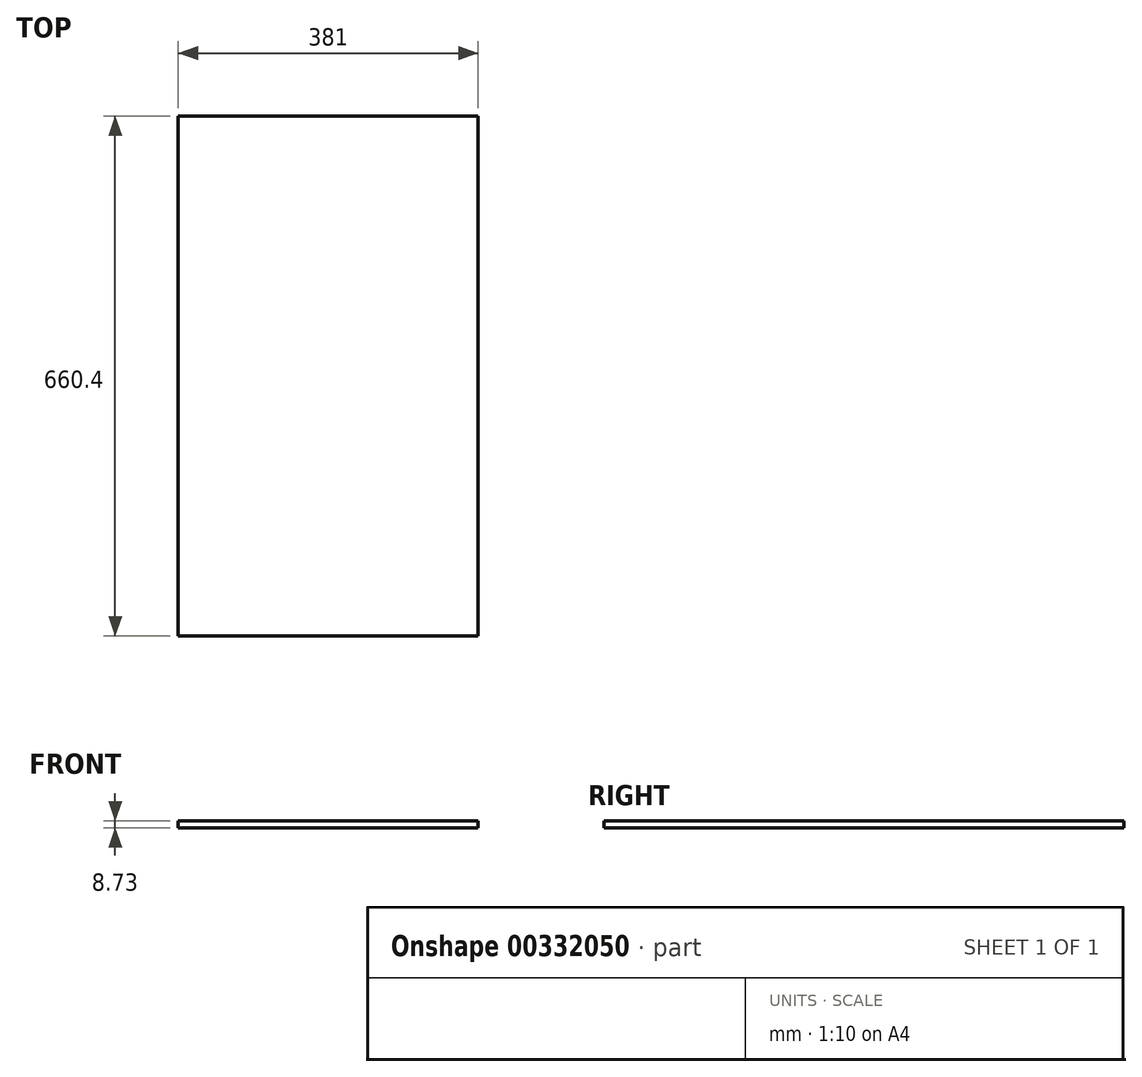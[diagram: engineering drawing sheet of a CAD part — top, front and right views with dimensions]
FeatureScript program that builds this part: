
annotation { "Feature Type Name" : "Feature", "Feature Type Description" : "" }
export const myFeature = defineFeature(function(context is Context, id is Id, definition is map)
    precondition{}
    {
        {
            var Q0;
            Q0=qCreatedBy(makeId("Top.planeOp"),FACE);
            var sketch = newSketch(context, id + "F0", { "sketchPlane" : qUnion([Q0])});
            skLineSegment(sketch, "E0.bottom", {"start": v(190.5, -330.2) * mm, "end": v(-190.5, -330.2) * mm});
            skLineSegment(sketch, "E0.top", {"start": v(190.5, 330.2) * mm, "end": v(-190.5, 330.2) * mm});
            skLineSegment(sketch, "E0.left", {"start": v(190.5, -330.2) * mm, "end": v(190.5, 330.2) * mm});
            skLineSegment(sketch, "E0.right", {"start": v(-190.5, -330.2) * mm, "end": v(-190.5, 330.2) * mm});
            skPoint(sketch, "E0.middle", {"position": v(0, 0) * mm});
            skLineSegment(sketch, "E1", {"start": v(-165.1, 330.2) * mm, "end": v(-165.1, 279.4) * mm});
            skLineSegment(sketch, "E2", {"start": v(-165.1, 279.4) * mm, "end": v(-190.5, 279.4) * mm});
            skLineSegment(sketch, "E3", {"start": v(-165.1, 279.4) * mm, "end": v(190.5, 184.12) * mm});
            skLineSegment(sketch, "E4", {"start": v(-165.1, 279.4) * mm, "end": v(190.5, 74.1) * mm});
            skPoint(sketch, "E5", {"position": v(-165.1, 303.85) * mm});
            skLineSegment(sketch, "E6", {"start": v(-165.1, 279.4) * mm, "end": v(190.5, -76.2) * mm});
            skLineSegment(sketch, "E7", {"start": v(-165.1, 279.4) * mm, "end": v(190.5, -336.52) * mm});
            skLineSegment(sketch, "E8", {"start": v(-165.1, 279.4) * mm, "end": v(-1.76, -330.2) * mm});
            skSolve(sketch);
        }
        {
            var Q0;
            Q0 = qSketchRegion(id + "F0", true);
            extrude(context, id + "F1", {"entities" : qUnion([Q0]), "depth" : 8.73 * mm});
        }
    });
